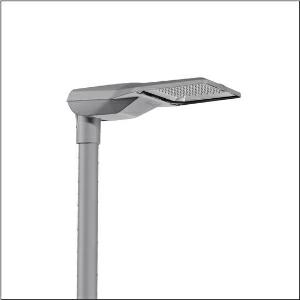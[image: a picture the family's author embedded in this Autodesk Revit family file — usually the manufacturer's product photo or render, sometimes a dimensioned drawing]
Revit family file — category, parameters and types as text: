
# Revit family: streetlight_sl_21_iq_midi___st1_0a_5xe3d31d08nb_3762
name_source: partatom
category: Lighting Fixtures
units: mm (PartAtom-declared; Revit-internal decimal feet)

## family parameters
Cut with Voids When Loaded = No
Host = Face
Light Source = No
Part Type = Normal
Room Calculation Point = No
Round Connector Dimension = Use Diameter
Shared = No

## types (1)
- --- (1 x LED, 23230 lm, 155.5 W, 3000K)
    Apparent Load = 155 VA
    CIE Flux Codes = 40 73 97 100 100
    Color Rendering = 70
    Color Temperature = 3000K
    Default Elevation = 1800 mm
    Description = Streetlight SL 21 iQ midi, mast luminaire, primary light control with lens, of PMMA, primary optical cover: cover, of toughened safety glass, transparent, light distribution: ST1.0a, light emission: direct distribution, primary light characteristic: asymmetric, installation type: post-top, side-entry, LED, High Power LED, rated luminous flux: 23.230lm, luminous efficacy: 149lm/W, light colour: 730, colour temperature: 3000K, control: Auto-Match, Temp-Guard, Lumen-Switch, Night-Set, Smart-Wire, Light-Fading, Desk-Remote (wireless, voltage-free reading and setting of iQ features in the workshop via application-optimized NFC function/RFID function), optimised constant luminous flux control (CLO 2.0), presetting dimming linear, mains connection: 230..240V, AC, 50/60Hz, start of lifetime: 156W, end of service life: 162W, reduction: 69W, luminaire housing, of diecast aluminium, powder-coated, Siteco® metallic grey (DB 702S), corrosivity category C5 mid according to DIN EN ISO 12944, please order mast flange separately, inclination adjustable: 0°, 5°, 10°, 15°, sealing non-destructively replaceable, multi-level sealing system, length: 644mm, width: 335mm, height: 110mm, mast flange for spigot size: 42mm (side-entry): 5XC10008XM4, 60/48mm (side-entry/post-top): 5XC10108XM2, 76/60mm (side-entry/post-top): 5XC10108XM1, protection rating (complete): IP66, insulation class (complete): insulation class II (safety insulation), certification: CE, ENEC, ENEC+, VDE, impact resistance: IK09, permissible operating ambient temperature for outdoor applications: -40..+50°C, standard-compliant lighting for roads and squares, packaging unit: 1 piece

Light Distribution: ST1.0a
    Height = 111 mm
    Lamp = 1 x LED
    Lamp Light Flux = 23230 lm
    Lamp Power = 155.5 W
    Lamp count = 1
    Length = 644 mm
    Luminous efficacy = 149 lm/W
    Manufacturer = Siteco
    ModVariant = No
    Model = 5XE3D31D08NB
    Number of Poles = 1
    OnlyDefault = Yes
    Power Factor = 1
    Product Name = Streetlight SL 21 iQ midi | ST1.0a
    Product group = mast luminaire | pylon top
    ProductGroupID = 6100
    Protection Class = Protection class II
    Protection Degree = IP 66
    RLX_Detail_Level = 1
    RLX_Emergency_Light_Flux = 0 lm
    RLX_Emergency_Type = 0
    RLX_Emergency_Type_DB = No
    RlxData = <blob elided: 90977 chars, md5=879f5427>
    Socket = socket
    Standby Power = 0 W
    System Light Flux = 23230 lm
    System Power = 155 W
    Type Comments = factory setting: luminous flux: 100 % | dim-lin: 254 | 823 mA
    Type Image = l_1004298.jpg
    URL = http://relux.com
    VarID = @adj_103623
    Voltage = 0 V
    Weight = 0.00 kg
    Width = 336 mm

## geometry (parser evidence)
native form markers: Blend x4, Sweep x11
no freeform markers — native parametric forms only
